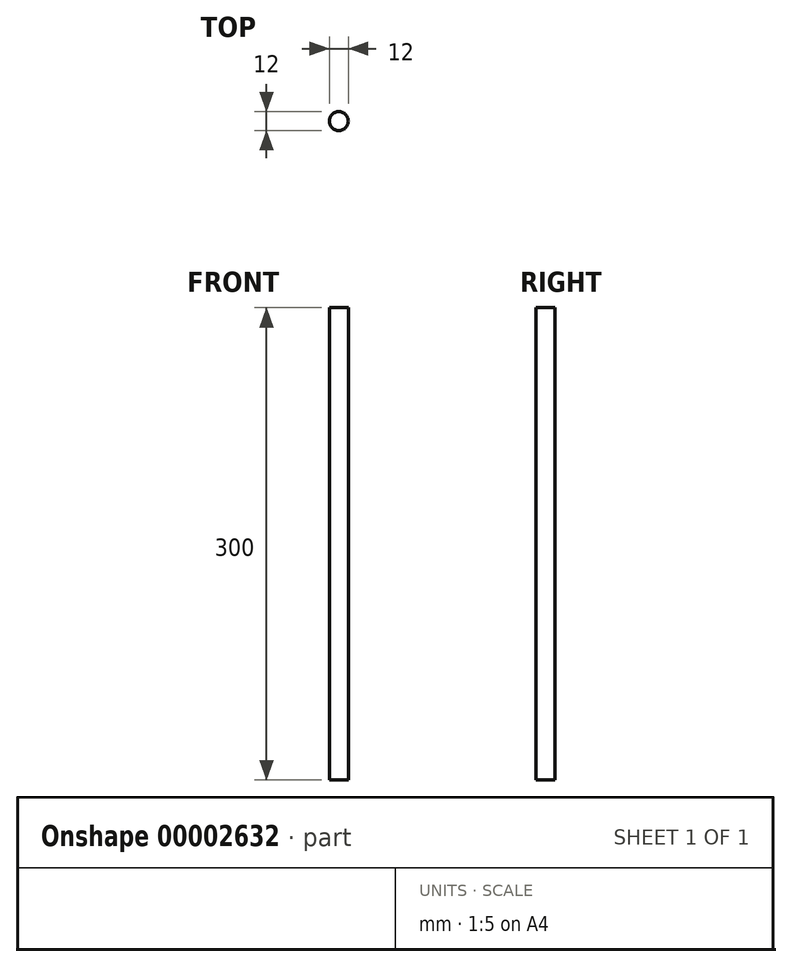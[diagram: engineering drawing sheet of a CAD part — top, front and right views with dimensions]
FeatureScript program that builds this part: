
annotation { "Feature Type Name" : "Feature", "Feature Type Description" : "" }
export const myFeature = defineFeature(function(context is Context, id is Id, definition is map)
    precondition{}
    {
        {
            var Q0;
            Q0=qCreatedBy(makeId("Top.planeOp"),FACE);
            var sketch = newSketch(context, id + "F0", { "sketchPlane" : qUnion([Q0])});
            skCircle(sketch, "E0", {"center": v(-46.64, -17.91) * mm, "radius": 6 * mm});
            skSolve(sketch);
        }
        {
            var Q0;
            Q0=makeQuery(id+"F0.imprint","IMPRINT",FACE,{"disambiguationData":[TD([[makeQuery(id+"F0.imprint","IMPRINT",EDGE,{"derivedFrom":sQuery(id+"F0.wireOp",EDGE,"E0")}),1.0]])]});
            extrude(context, id + "F1", {"entities" : qUnion([Q0]), "depth" : 300 * mm});
        }
    });
